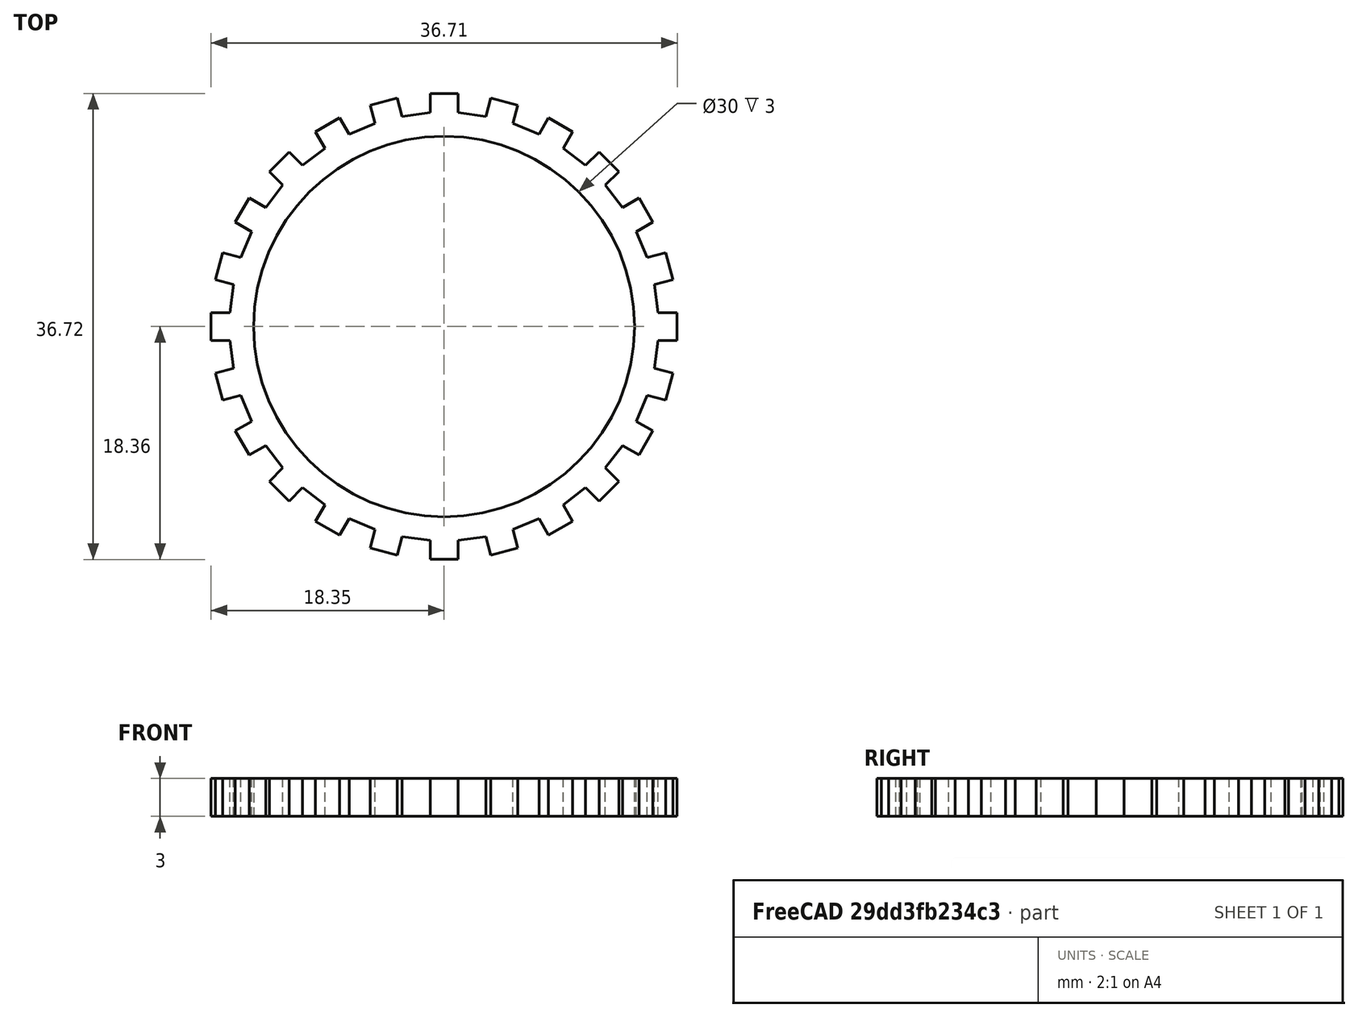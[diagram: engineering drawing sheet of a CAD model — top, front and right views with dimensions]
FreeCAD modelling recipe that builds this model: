
FCSTD DOCUMENT  (FreeCAD 0.19R24276 (Git))
Label: test_gear_1_1
License: All rights reserved
LicenseURL: http://en.wikipedia.org/wiki/All_rights_reserved
objects: Sketcher::SketchObject×1, PartDesign::Pad×1, PartDesign::Body×1
note: 4 computed .brp shape members not serialized (recipe doc carries the construction recipe); baked Part::Feature solids carry a one-line shape summary decoded from their .brp

FEATURE [Sketcher::SketchObject] Sketch
  FullyConstrained = false
  MapMode = 5
  Support = -> [XY_Plane]
  sketch-geometry (310):
    g0: Circle CenterX=0 CenterY=0 CenterZ=0 NormalX=0 NormalY=0 NormalZ=1 AngleXU=0 Radius=16.855
    g1: LineSegment StartX=0 StartY=16.855 StartZ=0 EndX=0 EndY=0 EndZ=0
    g2: LineSegment StartX=-4.3624 StartY=16.2807 StartZ=0 EndX=0 EndY=0 EndZ=0
    g3: LineSegment StartX=0 StartY=0 StartZ=0 EndX=4.3624 EndY=16.2807 EndZ=0
    g4: LineSegment StartX=0 StartY=0 StartZ=0 EndX=8.4275 EndY=14.5969 EndZ=0
    g5: LineSegment StartX=0 StartY=0 StartZ=0 EndX=11.9183 EndY=11.9183 EndZ=0
    g6: LineSegment StartX=0 StartY=0 StartZ=0 EndX=14.5969 EndY=8.4275 EndZ=0
    g7: LineSegment StartX=0 StartY=0 StartZ=0 EndX=16.2807 EndY=4.3624 EndZ=0
    g8: LineSegment StartX=0 StartY=0 StartZ=0 EndX=16.855 EndY=2.6e-15 EndZ=0
    g9: LineSegment StartX=-1.1 StartY=18.355 StartZ=0 EndX=-1.1 EndY=16.855 EndZ=0
    g10: LineSegment StartX=-1.1 StartY=16.855 StartZ=0 EndX=1.1 EndY=16.855 EndZ=0
    g11: LineSegment StartX=-1.1 StartY=18.355 StartZ=0 EndX=1.1 EndY=18.355 EndZ=0
    g12: GeomPoint X=0 Y=16.855 Z=0
    g13: LineSegment StartX=3.68811 StartY=18.0143 StartZ=0 EndX=3.29988 EndY=16.5654 EndZ=0
    g14: LineSegment StartX=3.29988 StartY=16.5654 StartZ=0 EndX=5.42491 EndY=15.996 EndZ=0
    g15: LineSegment StartX=3.68811 StartY=18.0143 StartZ=0 EndX=5.81314 EndY=17.4449 EndZ=0
    g16: LineSegment StartX=5.81314 StartY=17.4449 StartZ=0 EndX=5.42491 EndY=15.996 EndZ=0
    g17: GeomPoint X=4.3624 Y=16.2807 Z=0
    g18: LineSegment StartX=-10.1301 StartY=15.3459 StartZ=0 EndX=-9.38013 EndY=14.0469 EndZ=0
    g19: LineSegment StartX=-9.38013 StartY=14.0469 StartZ=0 EndX=-7.47487 EndY=15.1469 EndZ=0
    g20: LineSegment StartX=-10.1301 StartY=15.3459 StartZ=0 EndX=-8.22487 EndY=16.4459 EndZ=0
    g21: LineSegment StartX=-8.22487 StartY=16.4459 StartZ=0 EndX=-7.47487 EndY=15.1469 EndZ=0
    g22: GeomPoint X=-8.4275 Y=14.5969 Z=0
    g23: LineSegment StartX=0 StartY=0 StartZ=0 EndX=-8.4275 EndY=14.5969 EndZ=0
    g24: LineSegment StartX=-13.7568 StartY=12.2011 StartZ=0 EndX=-12.6961 EndY=11.1405 EndZ=0
    g25: LineSegment StartX=-12.6961 StartY=11.1405 StartZ=0 EndX=-11.1405 EndY=12.6961 EndZ=0
    g26: LineSegment StartX=-13.7568 StartY=12.2011 StartZ=0 EndX=-12.2011 EndY=13.7568 EndZ=0
    g27: LineSegment StartX=-12.2011 StartY=13.7568 StartZ=0 EndX=-11.1405 EndY=12.6961 EndZ=0
    g28: GeomPoint X=-11.9183 Y=11.9183 Z=0
    g29: LineSegment StartX=0 StartY=0 StartZ=0 EndX=-11.9183 EndY=11.9183 EndZ=0
    g30: LineSegment StartX=-5.81314 StartY=17.4449 StartZ=0 EndX=-5.42491 EndY=15.996 EndZ=0
    g31: LineSegment StartX=-5.42491 StartY=15.996 StartZ=0 EndX=-3.29988 EndY=16.5654 EndZ=0
    g32: LineSegment StartX=-5.81314 StartY=17.4449 StartZ=0 EndX=-3.68811 EndY=18.0143 EndZ=0
    g33: LineSegment StartX=-3.68811 StartY=18.0143 StartZ=0 EndX=-3.29988 EndY=16.5654 EndZ=0
    g34: GeomPoint X=-4.3624 Y=16.2807 Z=0
    g35: LineSegment StartX=8.22487 StartY=16.4459 StartZ=0 EndX=7.47487 EndY=15.1469 EndZ=0
    g36: LineSegment StartX=7.47487 StartY=15.1469 StartZ=0 EndX=9.38013 EndY=14.0469 EndZ=0
    g37: LineSegment StartX=8.22487 StartY=16.4459 StartZ=0 EndX=10.1301 EndY=15.3459 EndZ=0
    g38: LineSegment StartX=10.1301 StartY=15.3459 StartZ=0 EndX=9.38013 EndY=14.0469 EndZ=0
    g39: GeomPoint X=8.4275 Y=14.5969 Z=0
    g40: LineSegment StartX=12.2011 StartY=13.7568 StartZ=0 EndX=11.1405 EndY=12.6961 EndZ=0
    g41: LineSegment StartX=11.1405 StartY=12.6961 StartZ=0 EndX=12.6961 EndY=11.1405 EndZ=0
    g42: LineSegment StartX=12.2011 StartY=13.7568 StartZ=0 EndX=13.7568 EndY=12.2011 EndZ=0
    g43: LineSegment StartX=13.7568 StartY=12.2011 StartZ=0 EndX=12.6961 EndY=11.1405 EndZ=0
    g44: GeomPoint X=11.9183 Y=11.9183 Z=0
    g45: LineSegment StartX=15.3459 StartY=10.1301 StartZ=0 EndX=14.0469 EndY=9.38013 EndZ=0
    g46: LineSegment StartX=14.0469 StartY=9.38013 StartZ=0 EndX=15.1469 EndY=7.47487 EndZ=0
    g47: LineSegment StartX=15.3459 StartY=10.1301 StartZ=0 EndX=16.4459 EndY=8.22487 EndZ=0
    g48: LineSegment StartX=16.4459 StartY=8.22487 StartZ=0 EndX=15.1469 EndY=7.47487 EndZ=0
    g49: GeomPoint X=14.5969 Y=8.4275 Z=0
    g50: LineSegment StartX=17.4449 StartY=5.81314 StartZ=0 EndX=15.996 EndY=5.42491 EndZ=0
    g51: LineSegment StartX=15.996 StartY=5.42491 StartZ=0 EndX=16.5654 EndY=3.29988 EndZ=0
    g52: LineSegment StartX=17.4449 StartY=5.81314 StartZ=0 EndX=18.0143 EndY=3.68811 EndZ=0
    g53: LineSegment StartX=18.0143 StartY=3.68811 StartZ=0 EndX=16.5654 EndY=3.29988 EndZ=0
    g54: GeomPoint X=16.2807 Y=4.3624 Z=0
    g55: LineSegment StartX=0 StartY=0 StartZ=0 EndX=16.855 EndY=3.2e-15 EndZ=0
    g56: LineSegment StartX=18.355 StartY=1.1 StartZ=0 EndX=16.855 EndY=1.1 EndZ=0
    g57: LineSegment StartX=16.855 StartY=1.1 StartZ=0 EndX=16.855 EndY=-1.1 EndZ=0
    g58: LineSegment StartX=18.355 StartY=1.1 StartZ=0 EndX=18.355 EndY=-1.1 EndZ=0
    g59: LineSegment StartX=18.355 StartY=-1.1 StartZ=0 EndX=16.855 EndY=-1.1 EndZ=0
    g60: GeomPoint X=16.855 Y=3.2e-15 Z=0
    g61: LineSegment StartX=18.0143 StartY=-3.68811 StartZ=0 EndX=16.5654 EndY=-3.29988 EndZ=0
    g62: LineSegment StartX=16.5654 StartY=-3.29988 StartZ=0 EndX=15.996 EndY=-5.42491 EndZ=0
    g63: LineSegment StartX=18.0143 StartY=-3.68811 StartZ=0 EndX=17.4449 EndY=-5.81314 EndZ=0
    g64: LineSegment StartX=17.4449 StartY=-5.81314 StartZ=0 EndX=15.996 EndY=-5.42491 EndZ=0
    g65: GeomPoint X=16.2807 Y=-4.3624 Z=0
    g66: LineSegment StartX=0 StartY=0 StartZ=0 EndX=16.2807 EndY=-4.3624 EndZ=0
    g67: LineSegment StartX=16.4459 StartY=-8.22487 StartZ=0 EndX=15.1469 EndY=-7.47487 EndZ=0
    g68: LineSegment StartX=15.1469 StartY=-7.47487 StartZ=0 EndX=14.0469 EndY=-9.38013 EndZ=0
    g69: LineSegment StartX=16.4459 StartY=-8.22487 StartZ=0 EndX=15.3459 EndY=-10.1301 EndZ=0
    g70: LineSegment StartX=15.3459 StartY=-10.1301 StartZ=0 EndX=14.0469 EndY=-9.38013 EndZ=0
    g71: GeomPoint X=14.5969 Y=-8.4275 Z=0
    g72: LineSegment StartX=0 StartY=0 StartZ=0 EndX=14.5969 EndY=-8.4275 EndZ=0
    g73: LineSegment StartX=-16.4459 StartY=8.22487 StartZ=0 EndX=-15.1469 EndY=7.47487 EndZ=0
    g74: LineSegment StartX=-15.1469 StartY=7.47487 StartZ=0 EndX=-14.0469 EndY=9.38013 EndZ=0
    g75: LineSegment StartX=-16.4459 StartY=8.22487 StartZ=0 EndX=-15.3459 EndY=10.1301 EndZ=0
    g76: LineSegment StartX=-15.3459 StartY=10.1301 StartZ=0 EndX=-14.0469 EndY=9.38013 EndZ=0
    g77: GeomPoint X=-14.5969 Y=8.4275 Z=0
    g78: LineSegment StartX=0 StartY=0 StartZ=0 EndX=-14.5969 EndY=8.4275 EndZ=0
    g79: LineSegment StartX=-15.1469 StartY=7.47487 StartZ=0 EndX=-16.4459 EndY=8.22487 EndZ=0
    g80: LineSegment StartX=-16.4459 StartY=8.22487 StartZ=0 EndX=-15.3459 EndY=10.1301 EndZ=0
    g81: LineSegment StartX=-15.3459 StartY=10.1301 StartZ=0 EndX=-14.0469 EndY=9.38013 EndZ=0
    g82: LineSegment StartX=-12.6961 StartY=11.1405 StartZ=0 EndX=-14.0469 EndY=9.38013 EndZ=0
    g83: LineSegment StartX=-12.6961 StartY=11.1405 StartZ=0 EndX=-13.7568 EndY=12.2011 EndZ=0
    g84: LineSegment StartX=-13.7568 StartY=12.2011 StartZ=0 EndX=-12.2011 EndY=13.7568 EndZ=0
    g85: LineSegment StartX=-12.2011 StartY=13.7568 StartZ=0 EndX=-11.1405 EndY=12.6961 EndZ=0
    g86: LineSegment StartX=-11.1405 StartY=12.6961 StartZ=0 EndX=-9.38013 EndY=14.0469 EndZ=0
    g87: LineSegment StartX=-9.38013 StartY=14.0469 StartZ=0 EndX=-10.1301 EndY=15.3459 EndZ=0
    g88: LineSegment StartX=-10.1301 StartY=15.3459 StartZ=0 EndX=-8.22487 EndY=16.4459 EndZ=0
    g89: LineSegment StartX=-8.22487 StartY=16.4459 StartZ=0 EndX=-7.47487 EndY=15.1469 EndZ=0
    g90: LineSegment StartX=-7.47487 StartY=15.1469 StartZ=0 EndX=-5.42491 EndY=15.996 EndZ=0
    g91: LineSegment StartX=-5.42491 StartY=15.996 StartZ=0 EndX=-5.81314 EndY=17.4449 EndZ=0
    g92: LineSegment StartX=-5.81314 StartY=17.4449 StartZ=0 EndX=-3.68811 EndY=18.0143 EndZ=0
    g93: LineSegment StartX=-3.68811 StartY=18.0143 StartZ=0 EndX=-3.29988 EndY=16.5654 EndZ=0
    g94: LineSegment StartX=-3.29988 StartY=16.5654 StartZ=0 EndX=-1.1 EndY=16.855 EndZ=0
    g95: LineSegment StartX=-1.1 StartY=16.855 StartZ=0 EndX=-1.1 EndY=18.355 EndZ=0
    g96: LineSegment StartX=-1.1 StartY=18.355 StartZ=0 EndX=1.1 EndY=18.355 EndZ=0
    g97: LineSegment StartX=-18.0156 StartY=3.68811 StartZ=0 EndX=-16.5667 EndY=3.29988 EndZ=0
    g98: LineSegment StartX=-16.5667 StartY=3.29988 StartZ=0 EndX=-15.9973 EndY=5.42491 EndZ=0
    g99: LineSegment StartX=-18.0156 StartY=3.68811 StartZ=0 EndX=-17.4462 EndY=5.81314 EndZ=0
    g100: LineSegment StartX=-17.4462 StartY=5.81314 StartZ=0 EndX=-15.9973 EndY=5.42491 EndZ=0
    g101: GeomPoint X=-16.282 Y=4.3624 Z=0
    g102: LineSegment StartX=-0.00134425 StartY=1.8e-15 StartZ=0 EndX=-16.282 EndY=4.3624 EndZ=0
    g103: LineSegment StartX=-16.5667 StartY=3.29988 StartZ=0 EndX=-18.0156 EndY=3.68811 EndZ=0
    g104: LineSegment StartX=-18.0156 StartY=3.68811 StartZ=0 EndX=-17.4462 EndY=5.81314 EndZ=0
    g105: LineSegment StartX=-17.4462 StartY=5.81314 StartZ=0 EndX=-15.9973 EndY=5.42491 EndZ=0
    g106: LineSegment StartX=-18.3549 StartY=-1.1 StartZ=0 EndX=-16.8549 EndY=-1.1 EndZ=0
    g107: LineSegment StartX=-16.8549 StartY=-1.1 StartZ=0 EndX=-16.8549 EndY=1.1 EndZ=0
    g108: LineSegment StartX=-18.3549 StartY=-1.1 StartZ=0 EndX=-18.3549 EndY=1.1 EndZ=0
    g109: LineSegment StartX=-18.3549 StartY=1.1 StartZ=0 EndX=-16.8549 EndY=1.1 EndZ=0
    g110: GeomPoint X=-16.8549 Y=-6.7e-15 Z=0
    g111: LineSegment StartX=9.05985e-05 StartY=2.3e-15 StartZ=0 EndX=-16.8549 EndY=-6.7e-15 EndZ=0
    g112: LineSegment StartX=-18.3549 StartY=-1.1 StartZ=0 EndX=-18.3549 EndY=1.1 EndZ=0
    g113: LineSegment StartX=-18.3549 StartY=1.1 StartZ=0 EndX=-16.8549 EndY=1.1 EndZ=0
    g114: LineSegment StartX=-15.1469 StartY=7.47487 StartZ=0 EndX=-15.9973 EndY=5.42491 EndZ=0
    g115: LineSegment StartX=-16.5667 StartY=3.29988 StartZ=0 EndX=-16.8549 EndY=1.1 EndZ=0
    g116: LineSegment StartX=4.3624 StartY=16.2807 StartZ=0 EndX=0 EndY=0 EndZ=0
    g117: LineSegment StartX=1.1 StartY=18.355 StartZ=0 EndX=1.1 EndY=16.855 EndZ=0
    g118: GeomPoint X=0 Y=16.855 Z=0
    g119: LineSegment StartX=10.1301 StartY=15.3459 StartZ=0 EndX=9.38013 EndY=14.0469 EndZ=0
    g120: LineSegment StartX=9.38013 StartY=14.0469 StartZ=0 EndX=7.47487 EndY=15.1469 EndZ=0
    g121: LineSegment StartX=10.1301 StartY=15.3459 StartZ=0 EndX=8.22487 EndY=16.4459 EndZ=0
    g122: LineSegment StartX=8.22487 StartY=16.4459 StartZ=0 EndX=7.47487 EndY=15.1469 EndZ=0
    g123: GeomPoint X=8.4275 Y=14.5969 Z=0
    g124: LineSegment StartX=0 StartY=0 StartZ=0 EndX=8.4275 EndY=14.5969 EndZ=0
    g125: LineSegment StartX=13.7568 StartY=12.2011 StartZ=0 EndX=12.6961 EndY=11.1405 EndZ=0
    g126: LineSegment StartX=12.6961 StartY=11.1405 StartZ=0 EndX=11.1405 EndY=12.6961 EndZ=0
    g127: LineSegment StartX=13.7568 StartY=12.2011 StartZ=0 EndX=12.2011 EndY=13.7568 EndZ=0
    g128: LineSegment StartX=12.2011 StartY=13.7568 StartZ=0 EndX=11.1405 EndY=12.6961 EndZ=0
    g129: GeomPoint X=11.9183 Y=11.9183 Z=0
    g130: LineSegment StartX=0 StartY=0 StartZ=0 EndX=11.9183 EndY=11.9183 EndZ=0
    g131: LineSegment StartX=5.81314 StartY=17.4449 StartZ=0 EndX=5.42491 EndY=15.996 EndZ=0
    g132: LineSegment StartX=5.42491 StartY=15.996 StartZ=0 EndX=3.29988 EndY=16.5654 EndZ=0
    g133: LineSegment StartX=5.81314 StartY=17.4449 StartZ=0 EndX=3.68811 EndY=18.0143 EndZ=0
    g134: LineSegment StartX=3.68811 StartY=18.0143 StartZ=0 EndX=3.29988 EndY=16.5654 EndZ=0
    g135: GeomPoint X=4.3624 Y=16.2807 Z=0
    g136: LineSegment StartX=16.4459 StartY=8.22487 StartZ=0 EndX=15.1469 EndY=7.47487 EndZ=0
    g137: LineSegment StartX=15.1469 StartY=7.47487 StartZ=0 EndX=14.0469 EndY=9.38013 EndZ=0
    g138: LineSegment StartX=16.4459 StartY=8.22487 StartZ=0 EndX=15.3459 EndY=10.1301 EndZ=0
    g139: LineSegment StartX=15.3459 StartY=10.1301 StartZ=0 EndX=14.0469 EndY=9.38013 EndZ=0
    g140: GeomPoint X=14.5969 Y=8.4275 Z=0
    g141: LineSegment StartX=0 StartY=0 StartZ=0 EndX=14.5969 EndY=8.4275 EndZ=0
    g142: LineSegment StartX=15.1469 StartY=7.47487 StartZ=0 EndX=16.4459 EndY=8.22487 EndZ=0
    g143: LineSegment StartX=16.4459 StartY=8.22487 StartZ=0 EndX=15.3459 EndY=10.1301 EndZ=0
    g144: LineSegment StartX=15.3459 StartY=10.1301 StartZ=0 EndX=14.0469 EndY=9.38013 EndZ=0
    g145: LineSegment StartX=12.6961 StartY=11.1405 StartZ=0 EndX=14.0469 EndY=9.38013 EndZ=0
    g146: LineSegment StartX=12.6961 StartY=11.1405 StartZ=0 EndX=13.7568 EndY=12.2011 EndZ=0
    g147: LineSegment StartX=13.7568 StartY=12.2011 StartZ=0 EndX=12.2011 EndY=13.7568 EndZ=0
    g148: LineSegment StartX=12.2011 StartY=13.7568 StartZ=0 EndX=11.1405 EndY=12.6961 EndZ=0
    g149: LineSegment StartX=11.1405 StartY=12.6961 StartZ=0 EndX=9.38013 EndY=14.0469 EndZ=0
    g150: LineSegment StartX=9.38013 StartY=14.0469 StartZ=0 EndX=10.1301 EndY=15.3459 EndZ=0
    g151: LineSegment StartX=10.1301 StartY=15.3459 StartZ=0 EndX=8.22487 EndY=16.4459 EndZ=0
    g152: LineSegment StartX=8.22487 StartY=16.4459 StartZ=0 EndX=7.47487 EndY=15.1469 EndZ=0
    g153: LineSegment StartX=7.47487 StartY=15.1469 StartZ=0 EndX=5.42491 EndY=15.996 EndZ=0
    g154: LineSegment StartX=5.42491 StartY=15.996 StartZ=0 EndX=5.81314 EndY=17.4449 EndZ=0
    g155: LineSegment StartX=5.81314 StartY=17.4449 StartZ=0 EndX=3.68811 EndY=18.0143 EndZ=0
    g156: LineSegment StartX=3.68811 StartY=18.0143 StartZ=0 EndX=3.29988 EndY=16.5654 EndZ=0
    g157: LineSegment StartX=3.29988 StartY=16.5654 StartZ=0 EndX=1.1 EndY=16.855 EndZ=0
    g158: LineSegment StartX=18.0156 StartY=3.68811 StartZ=0 EndX=16.5667 EndY=3.29988 EndZ=0
    g159: LineSegment StartX=16.5667 StartY=3.29988 StartZ=0 EndX=15.9973 EndY=5.42491 EndZ=0
    g160: LineSegment StartX=18.0156 StartY=3.68811 StartZ=0 EndX=17.4462 EndY=5.81314 EndZ=0
    g161: LineSegment StartX=17.4462 StartY=5.81314 StartZ=0 EndX=15.9973 EndY=5.42491 EndZ=0
    g162: GeomPoint X=16.282 Y=4.3624 Z=0
    g163: LineSegment StartX=0.00134425 StartY=-1.2e-15 StartZ=0 EndX=16.282 EndY=4.3624 EndZ=0
    g164: LineSegment StartX=17.4462 StartY=5.81314 StartZ=0 EndX=15.9973 EndY=5.42491 EndZ=0
    g165: LineSegment StartX=18.3549 StartY=-1.1 StartZ=0 EndX=16.8549 EndY=-1.1 EndZ=0
    g166: LineSegment StartX=16.8549 StartY=-1.1 StartZ=0 EndX=16.8549 EndY=1.1 EndZ=0
    g167: LineSegment StartX=18.3549 StartY=-1.1 StartZ=0 EndX=18.3549 EndY=1.1 EndZ=0
    g168: LineSegment StartX=18.3549 StartY=1.1 StartZ=0 EndX=16.8549 EndY=1.1 EndZ=0
    g169: GeomPoint X=16.8549 Y=-7.1e-15 Z=0
    g170: LineSegment StartX=-9.05985e-05 StartY=1.7e-15 StartZ=0 EndX=16.8549 EndY=-7.1e-15 EndZ=0
    g171: LineSegment StartX=18.3549 StartY=1.1 StartZ=0 EndX=16.8549 EndY=1.1 EndZ=0
    g172: LineSegment StartX=15.1469 StartY=7.47487 StartZ=0 EndX=15.9973 EndY=5.42491 EndZ=0
    g173: LineSegment StartX=16.5667 StartY=3.29988 StartZ=0 EndX=16.8549 EndY=1.1 EndZ=0
    g174: LineSegment StartX=1.1 StartY=16.855 StartZ=0 EndX=1.1 EndY=18.355 EndZ=0
    g175: LineSegment StartX=-1.1 StartY=-18.355 StartZ=0 EndX=-1.1 EndY=-16.855 EndZ=0
    g176: LineSegment StartX=-1.1 StartY=-16.855 StartZ=0 EndX=1.1 EndY=-16.855 EndZ=0
    g177: LineSegment StartX=-1.1 StartY=-18.355 StartZ=0 EndX=1.1 EndY=-18.355 EndZ=0
    g178: GeomPoint X=1.08e-14 Y=-16.855 Z=0
    g179: LineSegment StartX=3.68811 StartY=-18.0143 StartZ=0 EndX=3.29988 EndY=-16.5654 EndZ=0
    g180: LineSegment StartX=3.29988 StartY=-16.5654 StartZ=0 EndX=5.42491 EndY=-15.996 EndZ=0
    g181: LineSegment StartX=3.68811 StartY=-18.0143 StartZ=0 EndX=5.81314 EndY=-17.4449 EndZ=0
    g182: LineSegment StartX=5.81314 StartY=-17.4449 StartZ=0 EndX=5.42491 EndY=-15.996 EndZ=0
    g183: GeomPoint X=4.3624 Y=-16.2807 Z=0
    g184: LineSegment StartX=-10.1301 StartY=-15.3459 StartZ=0 EndX=-9.38013 EndY=-14.0469 EndZ=0
    g185: LineSegment StartX=-9.38013 StartY=-14.0469 StartZ=0 EndX=-7.47487 EndY=-15.1469 EndZ=0
    g186: LineSegment StartX=-10.1301 StartY=-15.3459 StartZ=0 EndX=-8.22487 EndY=-16.4459 EndZ=0
    g187: LineSegment StartX=-8.22487 StartY=-16.4459 StartZ=0 EndX=-7.47487 EndY=-15.1469 EndZ=0
    g188: GeomPoint X=-8.4275 Y=-14.5969 Z=0
    g189: LineSegment StartX=-13.7568 StartY=-12.2011 StartZ=0 EndX=-12.6961 EndY=-11.1405 EndZ=0
    g190: LineSegment StartX=-12.6961 StartY=-11.1405 StartZ=0 EndX=-11.1405 EndY=-12.6961 EndZ=0
    g191: LineSegment StartX=-13.7568 StartY=-12.2011 StartZ=0 EndX=-12.2011 EndY=-13.7568 EndZ=0
    g192: LineSegment StartX=-12.2011 StartY=-13.7568 StartZ=0 EndX=-11.1405 EndY=-12.6961 EndZ=0
    g193: GeomPoint X=-11.9183 Y=-11.9183 Z=0
    g194: LineSegment StartX=-5.81314 StartY=-17.4449 StartZ=0 EndX=-5.42491 EndY=-15.996 EndZ=0
    g195: LineSegment StartX=-5.42491 StartY=-15.996 StartZ=0 EndX=-3.29988 EndY=-16.5654 EndZ=0
    g196: LineSegment StartX=-5.81314 StartY=-17.4449 StartZ=0 EndX=-3.68811 EndY=-18.0143 EndZ=0
    g197: LineSegment StartX=-3.68811 StartY=-18.0143 StartZ=0 EndX=-3.29988 EndY=-16.5654 EndZ=0
    g198: GeomPoint X=-4.3624 Y=-16.2807 Z=0
    g199: LineSegment StartX=8.22487 StartY=-16.4459 StartZ=0 EndX=7.47487 EndY=-15.1469 EndZ=0
    g200: LineSegment StartX=7.47487 StartY=-15.1469 StartZ=0 EndX=9.38013 EndY=-14.0469 EndZ=0
    g201: LineSegment StartX=8.22487 StartY=-16.4459 StartZ=0 EndX=10.1301 EndY=-15.3459 EndZ=0
    g202: LineSegment StartX=10.1301 StartY=-15.3459 StartZ=0 EndX=9.38013 EndY=-14.0469 EndZ=0
    g203: GeomPoint X=8.4275 Y=-14.5969 Z=0
    g204: LineSegment StartX=12.2011 StartY=-13.7568 StartZ=0 EndX=11.1405 EndY=-12.6961 EndZ=0
    g205: LineSegment StartX=11.1405 StartY=-12.6961 StartZ=0 EndX=12.6961 EndY=-11.1405 EndZ=0
    g206: LineSegment StartX=12.2011 StartY=-13.7568 StartZ=0 EndX=13.7568 EndY=-12.2011 EndZ=0
    g207: LineSegment StartX=13.7568 StartY=-12.2011 StartZ=0 EndX=12.6961 EndY=-11.1405 EndZ=0
    g208: GeomPoint X=11.9183 Y=-11.9183 Z=0
    g209: LineSegment StartX=15.3459 StartY=-10.1301 StartZ=0 EndX=14.0469 EndY=-9.38013 EndZ=0
    g210: LineSegment StartX=14.0469 StartY=-9.38013 StartZ=0 EndX=15.1469 EndY=-7.47487 EndZ=0
    g211: LineSegment StartX=15.3459 StartY=-10.1301 StartZ=0 EndX=16.4459 EndY=-8.22487 EndZ=0
    g212: LineSegment StartX=16.4459 StartY=-8.22487 StartZ=0 EndX=15.1469 EndY=-7.47487 EndZ=0
    g213: GeomPoint X=14.5969 Y=-8.4275 Z=0
    g214: LineSegment StartX=17.4449 StartY=-5.81314 StartZ=0 EndX=15.996 EndY=-5.42491 EndZ=0
    g215: LineSegment StartX=15.996 StartY=-5.42491 StartZ=0 EndX=16.5654 EndY=-3.29988 EndZ=0
    g216: LineSegment StartX=17.4449 StartY=-5.81314 StartZ=0 EndX=18.0143 EndY=-3.68811 EndZ=0
    g217: LineSegment StartX=18.0143 StartY=-3.68811 StartZ=0 EndX=16.5654 EndY=-3.29988 EndZ=0
    g218: GeomPoint X=16.2807 Y=-4.3624 Z=0
    g219: LineSegment StartX=18.355 StartY=-1.1 StartZ=0 EndX=16.855 EndY=-1.1 EndZ=0
    g220: LineSegment StartX=-16.4459 StartY=-8.22487 StartZ=0 EndX=-15.1469 EndY=-7.47487 EndZ=0
    g221: LineSegment StartX=-15.1469 StartY=-7.47487 StartZ=0 EndX=-14.0469 EndY=-9.38013 EndZ=0
    g222: LineSegment StartX=-16.4459 StartY=-8.22487 StartZ=0 EndX=-15.3459 EndY=-10.1301 EndZ=0
    g223: LineSegment StartX=-15.3459 StartY=-10.1301 StartZ=0 EndX=-14.0469 EndY=-9.38013 EndZ=0
    g224: GeomPoint X=-14.5969 Y=-8.4275 Z=0
    g225: LineSegment StartX=-15.1469 StartY=-7.47487 StartZ=0 EndX=-16.4459 EndY=-8.22487 EndZ=0
    g226: LineSegment StartX=-16.4459 StartY=-8.22487 StartZ=0 EndX=-15.3459 EndY=-10.1301 EndZ=0
    g227: LineSegment StartX=-15.3459 StartY=-10.1301 StartZ=0 EndX=-14.0469 EndY=-9.38013 EndZ=0
    g228: LineSegment StartX=-12.6961 StartY=-11.1405 StartZ=0 EndX=-14.0469 EndY=-9.38013 EndZ=0
    g229: LineSegment StartX=-12.6961 StartY=-11.1405 StartZ=0 EndX=-13.7568 EndY=-12.2011 EndZ=0
    g230: LineSegment StartX=-13.7568 StartY=-12.2011 StartZ=0 EndX=-12.2011 EndY=-13.7568 EndZ=0
    g231: LineSegment StartX=-12.2011 StartY=-13.7568 StartZ=0 EndX=-11.1405 EndY=-12.6961 EndZ=0
    g232: LineSegment StartX=-11.1405 StartY=-12.6961 StartZ=0 EndX=-9.38013 EndY=-14.0469 EndZ=0
    g233: LineSegment StartX=-9.38013 StartY=-14.0469 StartZ=0 EndX=-10.1301 EndY=-15.3459 EndZ=0
    g234: LineSegment StartX=-10.1301 StartY=-15.3459 StartZ=0 EndX=-8.22487 EndY=-16.4459 EndZ=0
    g235: LineSegment StartX=-8.22487 StartY=-16.4459 StartZ=0 EndX=-7.47487 EndY=-15.1469 EndZ=0
    g236: LineSegment StartX=-7.47487 StartY=-15.1469 StartZ=0 EndX=-5.42491 EndY=-15.996 EndZ=0
    g237: LineSegment StartX=-5.42491 StartY=-15.996 StartZ=0 EndX=-5.81314 EndY=-17.4449 EndZ=0
    g238: LineSegment StartX=-5.81314 StartY=-17.4449 StartZ=0 EndX=-3.68811 EndY=-18.0143 EndZ=0
    g239: LineSegment StartX=-3.68811 StartY=-18.0143 StartZ=0 EndX=-3.29988 EndY=-16.5654 EndZ=0
    g240: LineSegment StartX=-3.29988 StartY=-16.5654 StartZ=0 EndX=-1.1 EndY=-16.855 EndZ=0
    g241: LineSegment StartX=-1.1 StartY=-16.855 StartZ=0 EndX=-1.1 EndY=-18.355 EndZ=0
    g242: LineSegment StartX=-1.1 StartY=-18.355 StartZ=0 EndX=1.1 EndY=-18.355 EndZ=0
    g243: LineSegment StartX=-18.0156 StartY=-3.68811 StartZ=0 EndX=-16.5667 EndY=-3.29988 EndZ=0
    g244: LineSegment StartX=-16.5667 StartY=-3.29988 StartZ=0 EndX=-15.9973 EndY=-5.42491 EndZ=0
    g245: LineSegment StartX=-18.0156 StartY=-3.68811 StartZ=0 EndX=-17.4462 EndY=-5.81314 EndZ=0
    g246: LineSegment StartX=-17.4462 StartY=-5.81314 StartZ=0 EndX=-15.9973 EndY=-5.42491 EndZ=0
    g247: GeomPoint X=-16.282 Y=-4.3624 Z=0
    g248: LineSegment StartX=-16.5667 StartY=-3.29988 StartZ=0 EndX=-18.0156 EndY=-3.68811 EndZ=0
    g249: LineSegment StartX=-18.0156 StartY=-3.68811 StartZ=0 EndX=-17.4462 EndY=-5.81314 EndZ=0
    g250: LineSegment StartX=-17.4462 StartY=-5.81314 StartZ=0 EndX=-15.9973 EndY=-5.42491 EndZ=0
    g251: LineSegment StartX=-18.3549 StartY=-1.1 StartZ=0 EndX=-16.8549 EndY=-1.1 EndZ=0
    g252: LineSegment StartX=-18.3549 StartY=-1.1 StartZ=0 EndX=-16.8549 EndY=-1.1 EndZ=0
    g253: LineSegment StartX=-15.1469 StartY=-7.47487 StartZ=0 EndX=-15.9973 EndY=-5.42491 EndZ=0
    g254: LineSegment StartX=-16.5667 StartY=-3.29988 StartZ=0 EndX=-16.8549 EndY=-1.1 EndZ=0
    g255: LineSegment StartX=1.1 StartY=-18.355 StartZ=0 EndX=1.1 EndY=-16.855 EndZ=0
    g256: GeomPoint X=1.08e-14 Y=-16.855 Z=0
    g257: LineSegment StartX=10.1301 StartY=-15.3459 StartZ=0 EndX=9.38013 EndY=-14.0469 EndZ=0
    g258: LineSegment StartX=9.38013 StartY=-14.0469 StartZ=0 EndX=7.47487 EndY=-15.1469 EndZ=0
    g259: LineSegment StartX=10.1301 StartY=-15.3459 StartZ=0 EndX=8.22487 EndY=-16.4459 EndZ=0
    g260: LineSegment StartX=8.22487 StartY=-16.4459 StartZ=0 EndX=7.47487 EndY=-15.1469 EndZ=0
    g261: GeomPoint X=8.4275 Y=-14.5969 Z=0
    g262: LineSegment StartX=13.7568 StartY=-12.2011 StartZ=0 EndX=12.6961 EndY=-11.1405 EndZ=0
    g263: LineSegment StartX=12.6961 StartY=-11.1405 StartZ=0 EndX=11.1405 EndY=-12.6961 EndZ=0
    g264: LineSegment StartX=13.7568 StartY=-12.2011 StartZ=0 EndX=12.2011 EndY=-13.7568 EndZ=0
    g265: LineSegment StartX=12.2011 StartY=-13.7568 StartZ=0 EndX=11.1405 EndY=-12.6961 EndZ=0
    g266: GeomPoint X=11.9183 Y=-11.9183 Z=0
    g267: LineSegment StartX=5.81314 StartY=-17.4449 StartZ=0 EndX=5.42491 EndY=-15.996 EndZ=0
    g268: LineSegment StartX=5.42491 StartY=-15.996 StartZ=0 EndX=3.29988 EndY=-16.5654 EndZ=0
    g269: LineSegment StartX=5.81314 StartY=-17.4449 StartZ=0 EndX=3.68811 EndY=-18.0143 EndZ=0
    g270: LineSegment StartX=3.68811 StartY=-18.0143 StartZ=0 EndX=3.29988 EndY=-16.5654 EndZ=0
    g271: GeomPoint X=4.3624 Y=-16.2807 Z=0
    g272: LineSegment StartX=16.4459 StartY=-8.22487 StartZ=0 EndX=15.1469 EndY=-7.47487 EndZ=0
    g273: LineSegment StartX=15.1469 StartY=-7.47487 StartZ=0 EndX=14.0469 EndY=-9.38013 EndZ=0
    g274: LineSegment StartX=16.4459 StartY=-8.22487 StartZ=0 EndX=15.3459 EndY=-10.1301 EndZ=0
    g275: LineSegment StartX=15.3459 StartY=-10.1301 StartZ=0 EndX=14.0469 EndY=-9.38013 EndZ=0
    g276: GeomPoint X=14.5969 Y=-8.4275 Z=0
    g277: LineSegment StartX=15.1469 StartY=-7.47487 StartZ=0 EndX=16.4459 EndY=-8.22487 EndZ=0
    g278: LineSegment StartX=16.4459 StartY=-8.22487 StartZ=0 EndX=15.3459 EndY=-10.1301 EndZ=0
    g279: LineSegment StartX=15.3459 StartY=-10.1301 StartZ=0 EndX=14.0469 EndY=-9.38013 EndZ=0
    g280: LineSegment StartX=12.6961 StartY=-11.1405 StartZ=0 EndX=14.0469 EndY=-9.38013 EndZ=0
    g281: LineSegment StartX=12.6961 StartY=-11.1405 StartZ=0 EndX=13.7568 EndY=-12.2011 EndZ=0
    g282: LineSegment StartX=13.7568 StartY=-12.2011 StartZ=0 EndX=12.2011 EndY=-13.7568 EndZ=0
    g283: LineSegment StartX=12.2011 StartY=-13.7568 StartZ=0 EndX=11.1405 EndY=-12.6961 EndZ=0
    g284: LineSegment StartX=11.1405 StartY=-12.6961 StartZ=0 EndX=9.38013 EndY=-14.0469 EndZ=0
    g285: LineSegment StartX=9.38013 StartY=-14.0469 StartZ=0 EndX=10.1301 EndY=-15.3459 EndZ=0
    g286: LineSegment StartX=10.1301 StartY=-15.3459 StartZ=0 EndX=8.22487 EndY=-16.4459 EndZ=0
    g287: LineSegment StartX=8.22487 StartY=-16.4459 StartZ=0 EndX=7.47487 EndY=-15.1469 EndZ=0
    g288: LineSegment StartX=7.47487 StartY=-15.1469 StartZ=0 EndX=5.42491 EndY=-15.996 EndZ=0
    g289: LineSegment StartX=5.42491 StartY=-15.996 StartZ=0 EndX=5.81314 EndY=-17.4449 EndZ=0
    g290: LineSegment StartX=5.81314 StartY=-17.4449 StartZ=0 EndX=3.68811 EndY=-18.0143 EndZ=0
    g291: LineSegment StartX=3.68811 StartY=-18.0143 StartZ=0 EndX=3.29988 EndY=-16.5654 EndZ=0
    g292: LineSegment StartX=3.29988 StartY=-16.5654 StartZ=0 EndX=1.1 EndY=-16.855 EndZ=0
    g293: LineSegment StartX=18.0156 StartY=-3.68811 StartZ=0 EndX=16.5667 EndY=-3.29988 EndZ=0
    g294: LineSegment StartX=16.5667 StartY=-3.29988 StartZ=0 EndX=15.9973 EndY=-5.42491 EndZ=0
    g295: LineSegment StartX=18.0156 StartY=-3.68811 StartZ=0 EndX=17.4462 EndY=-5.81314 EndZ=0
    g296: LineSegment StartX=17.4462 StartY=-5.81314 StartZ=0 EndX=15.9973 EndY=-5.42491 EndZ=0
    g297: GeomPoint X=16.282 Y=-4.3624 Z=0
    g298: LineSegment StartX=16.5667 StartY=-3.29988 StartZ=0 EndX=18.0156 EndY=-3.68811 EndZ=0
    g299: LineSegment StartX=18.0156 StartY=-3.68811 StartZ=0 EndX=17.4462 EndY=-5.81314 EndZ=0
    g300: LineSegment StartX=17.4462 StartY=-5.81314 StartZ=0 EndX=15.9973 EndY=-5.42491 EndZ=0
    g301: LineSegment StartX=18.3549 StartY=-1.1 StartZ=0 EndX=16.8549 EndY=-1.1 EndZ=0
    g302: LineSegment StartX=15.1469 StartY=-7.47487 StartZ=0 EndX=15.9973 EndY=-5.42491 EndZ=0
    g303: LineSegment StartX=16.5667 StartY=-3.29988 StartZ=0 EndX=16.8549 EndY=-1.1 EndZ=0
    g304: LineSegment StartX=1.1 StartY=-16.855 StartZ=0 EndX=1.1 EndY=-18.355 EndZ=0
    g305: Circle CenterX=0 CenterY=0 CenterZ=0 NormalX=0 NormalY=0 NormalZ=1 AngleXU=0 Radius=15
    g306: LineSegment StartX=18.0156 StartY=3.68811 StartZ=0 EndX=16.5667 EndY=3.29988 EndZ=0
    g307: LineSegment StartX=17.4462 StartY=5.81314 StartZ=0 EndX=18.0156 EndY=3.68811 EndZ=0
    g308: LineSegment StartX=18.3549 StartY=1.1 StartZ=0 EndX=18.355 EndY=-1.1 EndZ=0
    g309: LineSegment StartX=18.355 StartY=-1.1 StartZ=0 EndX=16.8549 EndY=-1.1 EndZ=0
  constraints (689):
    c: Diameter(g0) = 33.71
    c: Vertical(g1)
    c: Coincident(g0,g-1)
    c: Coincident(g1,g0)
    c: Coincident(g2,g0)
    c: Angle(g1,g2) = 0.261799
    c: Coincident(g3,g0)
    c: Angle(g3,g1) = 0.261799
    c: PointOnObject(g3,g0)
    c: PointOnObject(g1,g0)
    c: PointOnObject(g2,g0)
    c: Coincident(g4,g0)
    c: Angle(g4,g3) = 0.261799
    c: PointOnObject(g4,g0)
    c: Coincident(g5,g0)
    c: Angle(g5,g4) = 0.261799
    c: Coincident(g6,g0)
    c: Angle(g6,g5) = 0.261799
    c: Coincident(g7,g0)
    c: Angle(g7,g6) = 0.261799
    c: Coincident(g8,g0)
    c: Angle(g8,g7) = 0.261799
    c: PointOnObject(g5,g0)
    c: PointOnObject(g7,g0)
    c: PointOnObject(g6,g0)
    c: PointOnObject(g8,g0)
    c: Coincident(g10,g9)
    c: Coincident(g11,g9)
    c: Parallel(g10,g11)
    c: Perpendicular(g10,g9)
    c: Distance(g9,g11) = 2.2
    c: Distance(g11,g10) = 1.5
    c: PointOnObject(g12,g10)
    c: Distance(g9,g12) = 1.1
    c: Coincident(g12,g1)
    c: Perpendicular(g1,g10)
    c: Coincident(g14,g13)
    c: Coincident(g15,g13)
    c: Coincident(g16,g15)
    c: Coincident(g16,g14)
    c: Parallel(g14,g15)
    c: Parallel(g13,g16)
    c: Perpendicular(g14,g13)
    c: Distance(g13,g15) = 2.2
    c: Distance(g15,g14) = 1.5
    c: PointOnObject(g17,g14)
    c: Distance(g13,g17) = 1.1
    c: Coincident(g17,g3)
    c: Perpendicular(g3,g14)
    c: Coincident(g19,g18)
    c: Coincident(g20,g18)
    c: Coincident(g21,g20)
    c: Coincident(g21,g19)
    c: Parallel(g19,g20)
    c: Parallel(g18,g21)
    c: Perpendicular(g19,g18)
    c: Distance(g18,g20) = 2.2
    c: Distance(g20,g19) = 1.5
    c: PointOnObject(g22,g19)
    c: Distance(g18,g22) = 1.1
    c: Perpendicular(g23,g19)
    c: Coincident(g23,g0)
    c: Angle(g23,g2) = -0.261799
    c: PointOnObject(g23,g0)
    c: Coincident(g22,g23)
    c: Coincident(g25,g24)
    c: Coincident(g26,g24)
    c: Coincident(g27,g26)
    c: Coincident(g27,g25)
    c: Parallel(g25,g26)
    c: Parallel(g24,g27)
    c: Perpendicular(g25,g24)
    c: Distance(g24,g26) = 2.2
    c: Distance(g26,g25) = 1.5
    c: PointOnObject(g28,g25)
    c: Distance(g24,g28) = 1.1
    c: Perpendicular(g29,g25)
    c: Coincident(g28,g29)
    c: Equal(g29,g23)
    c: Coincident(g29,g0)
    c: Angle(g23,g29) = 0.261799
    c: Coincident(g31,g30)
    c: Coincident(g32,g30)
    c: Coincident(g33,g32)
    c: Coincident(g33,g31)
    c: Parallel(g31,g32)
    c: Parallel(g30,g33)
    c: Perpendicular(g31,g30)
    c: Distance(g30,g32) = 2.2
    c: Distance(g32,g31) = 1.5
    c: PointOnObject(g34,g31)
    c: Distance(g30,g34) = 1.1
    c: Coincident(g34,g2)
    c: Perpendicular(g2,g31)
    c: Coincident(g36,g35)
    c: Coincident(g37,g35)
    c: Coincident(g38,g37)
    c: Coincident(g38,g36)
    c: Parallel(g36,g37)
    c: Parallel(g35,g38)
    c: Perpendicular(g36,g35)
    c: Distance(g35,g37) = 2.2
    c: Distance(g37,g36) = 1.5
    c: PointOnObject(g39,g36)
    c: Distance(g35,g39) = 1.1
    c: Coincident(g39,g4)
    c: Perpendicular(g4,g36)
    c: Coincident(g41,g40)
    c: Coincident(g42,g40)
    c: Coincident(g43,g42)
    c: Coincident(g43,g41)
    c: Parallel(g41,g42)
    c: Parallel(g40,g43)
    c: Perpendicular(g41,g40)
    c: Distance(g40,g42) = 2.2
    c: Distance(g42,g41) = 1.5
    c: PointOnObject(g44,g41)
    c: Distance(g40,g44) = 1.1
    c: Coincident(g5,g44)
    c: Perpendicular(g5,g41)
    c: Coincident(g46,g45)
    c: Coincident(g47,g45)
    c: Coincident(g48,g47)
    c: Coincident(g48,g46)
    c: Parallel(g46,g47)
    c: Parallel(g45,g48)
    c: Perpendicular(g46,g45)
    c: Distance(g45,g47) = 2.2
    c: Distance(g47,g46) = 1.5
    c: PointOnObject(g49,g46)
    c: Distance(g45,g49) = 1.1
    c: Coincident(g49,g6)
    c: Perpendicular(g46,g6)
    c: Coincident(g51,g50)
    c: Coincident(g52,g50)
    c: Coincident(g53,g52)
    c: Coincident(g53,g51)
    c: Parallel(g51,g52)
    c: Parallel(g50,g53)
    c: Perpendicular(g51,g50)
    c: Distance(g50,g52) = 2.2
    c: Distance(g52,g51) = 1.5
    c: PointOnObject(g54,g51)
    c: Distance(g50,g54) = 1.1
    c: Coincident(g54,g7)
    c: Perpendicular(g7,g51)
    c: Coincident(g57,g56)
    c: Coincident(g58,g56)
    c: Coincident(g59,g58)
    c: Coincident(g59,g57)
    c: Parallel(g57,g58)
    c: Parallel(g56,g59)
    c: Perpendicular(g57,g56)
    c: Distance(g56,g58) = 2.2
    c: Distance(g58,g57) = 1.5
    c: PointOnObject(g60,g57)
    c: Distance(g56,g60) = 1.1
    c: Coincident(g60,g55)
    c: Perpendicular(g55,g57)
    c: Equal(g55,g7)
    c: Coincident(g55,g0)
    c: Angle(g55,g7) = 0.261799
    c: Coincident(g62,g61)
    c: Coincident(g63,g61)
    c: Coincident(g64,g63)
    c: Coincident(g64,g62)
    c: Parallel(g62,g63)
    c: Parallel(g61,g64)
    c: Perpendicular(g62,g61)
    c: Distance(g61,g63) = 2.2
    c: Distance(g63,g62) = 1.5
    c: PointOnObject(g65,g62)
    c: Distance(g61,g65) = 1.1
    c: Equal(g7,g66)
    c: Coincident(g66,g65)
    c: Perpendicular(g62,g66)
    c: Coincident(g66,g0)
    c: Angle(g66,g8) = 0.261799
    c: Coincident(g68,g67)
    c: Coincident(g69,g67)
    c: Coincident(g70,g69)
    c: Coincident(g70,g68)
    c: Parallel(g68,g69)
    c: Parallel(g67,g70)
    c: Perpendicular(g68,g67)
    c: Distance(g67,g69) = 2.2
    c: Distance(g69,g68) = 1.5
    c: PointOnObject(g71,g68)
    c: Distance(g67,g71) = 1.1
    c: Perpendicular(g72,g68)
    c: Coincident(g71,g72)
    c: Equal(g72,g66)
    c: Coincident(g72,g0)
    c: Angle(g72,g66) = 0.261799
    c: Coincident(g74,g73)
    c: Coincident(g75,g73)
    c: Coincident(g76,g75)
    c: Coincident(g76,g74)
    c: Parallel(g74,g75)
    c: Parallel(g73,g76)
    c: Perpendicular(g74,g73)
    c: Distance(g73,g75) = 2.2
    c: Distance(g75,g74) = 1.5
    c: PointOnObject(g77,g74)
    c: Distance(g73,g77) = 1.1
    c: Perpendicular(g78,g74)
    c: Coincident(g77,g78)
    c: Equal(g29,g78)
    c: Coincident(g78,g0)
    c: Angle(g29,g78) = 0.261799
    c: Coincident(g79,g73)
    c: Coincident(g79,g73)
    c: Coincident(g80,g79)
    c: Coincident(g80,g75)
    c: Coincident(g81,g80)
    c: Coincident(g81,g74)
    c: Coincident(g82,g24)
    c: Coincident(g82,g81)
    c: Coincident(g83,g82)
    c: Coincident(g83,g24)
    c: Coincident(g84,g83)
    c: Coincident(g84,g26)
    c: Coincident(g85,g84)
    c: Coincident(g85,g25)
    c: Coincident(g86,g85)
    c: Coincident(g86,g18)
    c: Coincident(g87,g86)
    c: Coincident(g87,g18)
    c: Coincident(g88,g87)
    c: Coincident(g88,g20)
    c: Coincident(g89,g88)
    c: Coincident(g89,g19)
    c: Coincident(g90,g89)
    c: Coincident(g90,g30)
    c: Coincident(g91,g90)
    c: Coincident(g91,g30)
    c: Coincident(g92,g91)
    c: Coincident(g92,g32)
    c: Coincident(g93,g92)
    c: Coincident(g93,g31)
    c: Coincident(g94,g93)
    c: Coincident(g94,g9)
    c: Coincident(g95,g94)
    c: PointOnObject(g95,g11)
    c: Vertical(g95)
    c: Coincident(g96,g95)
    c: Coincident(g96,g11)
    c: Coincident(g98,g97)
    c: Coincident(g99,g97)
    c: Coincident(g100,g99)
    c: Coincident(g100,g98)
    c: Parallel(g98,g99)
    c: Parallel(g97,g100)
    c: Perpendicular(g98,g97)
    c: Distance(g97,g99) = 2.2
    c: Distance(g99,g98) = 1.5
    c: PointOnObject(g101,g98)
    c: Distance(g97,g101) = 1.1
    c: Perpendicular(g102,g98)
    c: Coincident(g101,g102)
    c: Coincident(g103,g97)
    c: Coincident(g103,g97)
    c: Coincident(g104,g103)
    c: Coincident(g104,g99)
    c: Coincident(g105,g104)
    c: Coincident(g105,g98)
    c: Equal(g102,g78)
    c: Angle(g78,g102) = 0.261799
    c: Coincident(g107,g106)
    c: Coincident(g108,g106)
    c: Coincident(g109,g108)
    c: Coincident(g109,g107)
    c: Parallel(g107,g108)
    c: Parallel(g106,g109)
    c: Perpendicular(g107,g106)
    c: Distance(g106,g108) = 2.2
    c: Distance(g108,g107) = 1.5
    c: PointOnObject(g110,g107)
    c: Distance(g106,g110) = 1.1
    c: Perpendicular(g111,g107)
    c: Coincident(g110,g111)
    c: Coincident(g112,g108)
    c: Coincident(g113,g112)
    c: Coincident(g113,g107)
    c: Equal(g111,g102)
    c: Angle(g102,g111) = 0.261799
    c: Coincident(g114,g79)
    c: Coincident(g114,g105)
    c: Coincident(g115,g103)
    c: Coincident(g115,g113)
    c: Distance(g117,g118) = 1.1
    c: Coincident(g120,g119)
    c: Coincident(g121,g119)
    c: Coincident(g122,g121)
    c: Coincident(g122,g120)
    c: Parallel(g120,g121)
    c: Parallel(g119,g122)
    c: Perpendicular(g120,g119)
    c: Distance(g119,g121) = 2.2
    c: Distance(g121,g120) = 1.5
    c: PointOnObject(g123,g120)
    c: Distance(g119,g123) = 1.1
    c: Perpendicular(g124,g120)
    c: Angle(g124,g116) = 0.261799
    c: Coincident(g123,g124)
    c: Coincident(g126,g125)
    c: Coincident(g127,g125)
    c: Coincident(g128,g127)
    c: Coincident(g128,g126)
    c: Parallel(g126,g127)
    c: Parallel(g125,g128)
    c: Perpendicular(g126,g125)
    c: Distance(g125,g127) = 2.2
    c: Distance(g127,g126) = 1.5
    c: PointOnObject(g129,g126)
    c: Distance(g125,g129) = 1.1
    c: Perpendicular(g130,g126)
    c: Coincident(g129,g130)
    c: Equal(g130,g124)
    c: Angle(g124,g130) = -0.261799
    c: Coincident(g132,g131)
    c: Coincident(g133,g131)
    c: Coincident(g134,g133)
    c: Coincident(g134,g132)
    c: Parallel(g132,g133)
    c: Parallel(g131,g134)
    c: Perpendicular(g132,g131)
    c: Distance(g131,g133) = 2.2
    c: Distance(g133,g132) = 1.5
    c: PointOnObject(g135,g132)
    c: Distance(g131,g135) = 1.1
    c: Coincident(g135,g116)
    c: Perpendicular(g116,g132)
    c: Coincident(g137,g136)
    c: Coincident(g138,g136)
    c: Coincident(g139,g138)
    c: Coincident(g139,g137)
    c: Parallel(g137,g138)
    c: Parallel(g136,g139)
    c: Perpendicular(g137,g136)
    c: Distance(g136,g138) = 2.2
    c: Distance(g138,g137) = 1.5
    c: PointOnObject(g140,g137)
    c: Distance(g136,g140) = 1.1
    c: Perpendicular(g141,g137)
    c: Coincident(g140,g141)
    c: Equal(g130,g141)
    c: Angle(g130,g141) = -0.261799
    c: Coincident(g142,g136)
    c: Coincident(g142,g136)
    c: Coincident(g143,g142)
    c: Coincident(g143,g138)
    c: Coincident(g144,g143)
    c: Coincident(g144,g137)
    c: Coincident(g145,g125)
    c: Coincident(g145,g144)
    c: Coincident(g146,g145)
    c: Coincident(g146,g125)
    c: Coincident(g147,g146)
    c: Coincident(g147,g127)
    c: Coincident(g148,g147)
    c: Coincident(g148,g126)
    c: Coincident(g149,g148)
    c: Coincident(g149,g119)
    c: Coincident(g150,g149)
    c: Coincident(g150,g119)
    c: Coincident(g151,g150)
    c: Coincident(g151,g121)
    c: Coincident(g152,g151)
    c: Coincident(g152,g120)
    c: Coincident(g153,g152)
    c: Coincident(g153,g131)
    c: Coincident(g154,g153)
    c: Coincident(g154,g131)
    c: Coincident(g155,g154)
    c: Coincident(g155,g133)
    c: Coincident(g156,g155)
    c: Coincident(g156,g132)
    c: Coincident(g157,g156)
    c: Coincident(g157,g117)
    c: Coincident(g159,g158)
    c: Coincident(g160,g158)
    c: Coincident(g161,g160)
    c: Coincident(g161,g159)
    c: Parallel(g159,g160)
    c: Parallel(g158,g161)
    c: Perpendicular(g159,g158)
    c: Distance(g158,g160) = 2.2
    c: Distance(g160,g159) = 1.5
    c: PointOnObject(g162,g159)
    c: Distance(g158,g162) = 1.1
    c: Perpendicular(g163,g159)
    c: Coincident(g162,g163)
    c: Coincident(g164,g159)
    c: Equal(g163,g141)
    c: Angle(g141,g163) = -0.261799
    c: Coincident(g166,g165)
    c: Coincident(g167,g165)
    c: Coincident(g168,g167)
    c: Coincident(g168,g166)
    c: Parallel(g166,g167)
    c: Parallel(g165,g168)
    c: Perpendicular(g166,g165)
    c: Distance(g165,g167) = 2.2
    c: Distance(g167,g166) = 1.5
    c: PointOnObject(g169,g166)
    c: Distance(g165,g169) = 1.1
    c: Perpendicular(g170,g166)
    c: Coincident(g169,g170)
    c: Coincident(g171,g166)
    c: Equal(g170,g163)
    c: Angle(g163,g170) = -0.261799
    c: Coincident(g172,g142)
    c: Coincident(g172,g164)
    c: Coincident(g173,g171)
    c: Coincident(g174,g157)
    c: Coincident(g96,g174)
    c: Coincident(g176,g175)
    c: Coincident(g177,g175)
    c: Parallel(g176,g177)
    c: Perpendicular(g176,g175)
    c: Distance(g175,g177) = 2.2
    c: Distance(g177,g176) = 1.5
    c: PointOnObject(g178,g176)
    c: Distance(g175,g178) = 1.1
    c: Coincident(g180,g179)
    c: Coincident(g181,g179)
    c: Coincident(g182,g181)
    c: Coincident(g182,g180)
    c: Parallel(g180,g181)
    c: Parallel(g179,g182)
    c: Perpendicular(g180,g179)
    c: Distance(g179,g181) = 2.2
    c: Distance(g181,g180) = 1.5
    c: PointOnObject(g183,g180)
    c: Distance(g179,g183) = 1.1
    c: Coincident(g185,g184)
    c: Coincident(g186,g184)
    c: Coincident(g187,g186)
    c: Coincident(g187,g185)
    c: Parallel(g185,g186)
    c: Parallel(g184,g187)
    c: Perpendicular(g185,g184)
    c: Distance(g184,g186) = 2.2
    c: Distance(g186,g185) = 1.5
    c: PointOnObject(g188,g185)
    c: Distance(g184,g188) = 1.1
    c: Coincident(g190,g189)
    c: Coincident(g191,g189)
    c: Coincident(g192,g191)
    c: Coincident(g192,g190)
    c: Parallel(g190,g191)
    c: Parallel(g189,g192)
    c: Perpendicular(g190,g189)
    c: Distance(g189,g191) = 2.2
    c: Distance(g191,g190) = 1.5
    c: PointOnObject(g193,g190)
    c: Distance(g189,g193) = 1.1
    c: Coincident(g195,g194)
    c: Coincident(g196,g194)
    c: Coincident(g197,g196)
    c: Coincident(g197,g195)
    c: Parallel(g195,g196)
    c: Parallel(g194,g197)
    c: Perpendicular(g195,g194)
    c: Distance(g194,g196) = 2.2
    c: Distance(g196,g195) = 1.5
    c: PointOnObject(g198,g195)
    c: Distance(g194,g198) = 1.1
    c: Coincident(g200,g199)
    c: Coincident(g201,g199)
    c: Coincident(g202,g201)
    c: Coincident(g202,g200)
    c: Parallel(g200,g201)
    c: Parallel(g199,g202)
    c: Perpendicular(g200,g199)
    c: Distance(g199,g201) = 2.2
    c: Distance(g201,g200) = 1.5
    c: PointOnObject(g203,g200)
    c: Distance(g199,g203) = 1.1
    c: Coincident(g205,g204)
    c: Coincident(g206,g204)
    c: Coincident(g207,g206)
    c: Coincident(g207,g205)
    c: Parallel(g205,g206)
    c: Parallel(g204,g207)
    c: Perpendicular(g205,g204)
    c: Distance(g204,g206) = 2.2
    c: Distance(g206,g205) = 1.5
    c: PointOnObject(g208,g205)
    c: Distance(g204,g208) = 1.1
    c: Coincident(g210,g209)
    c: Coincident(g211,g209)
    c: Coincident(g212,g211)
    c: Coincident(g212,g210)
    c: Parallel(g210,g211)
    c: Parallel(g209,g212)
    c: Perpendicular(g210,g209)
    c: Distance(g209,g211) = 2.2
    c: Distance(g211,g210) = 1.5
    c: PointOnObject(g213,g210)
    c: Distance(g209,g213) = 1.1
    c: Coincident(g215,g214)
    c: Coincident(g216,g214)
    c: Coincident(g217,g216)
    c: Coincident(g217,g215)
    c: Parallel(g215,g216)
    c: Parallel(g214,g217)
    c: Perpendicular(g215,g214)
    c: Distance(g214,g216) = 2.2
    c: Distance(g216,g215) = 1.5
    c: PointOnObject(g218,g215)
    c: Distance(g214,g218) = 1.1
    c: Coincident(g221,g220)
    c: Coincident(g222,g220)
    c: Coincident(g223,g222)
    c: Coincident(g223,g221)
    c: Parallel(g221,g222)
    c: Parallel(g220,g223)
    c: Perpendicular(g221,g220)
    c: Distance(g220,g222) = 2.2
    c: Distance(g222,g221) = 1.5
    c: PointOnObject(g224,g221)
    c: Distance(g220,g224) = 1.1
    c: Coincident(g225,g220)
    c: Coincident(g225,g220)
    c: Coincident(g226,g225)
    c: Coincident(g226,g222)
    c: Coincident(g227,g226)
    c: Coincident(g227,g221)
    c: Coincident(g228,g189)
    c: Coincident(g228,g227)
    c: Coincident(g229,g228)
    c: Coincident(g229,g189)
    c: Coincident(g230,g229)
    c: Coincident(g230,g191)
    c: Coincident(g231,g230)
    c: Coincident(g231,g190)
    c: Coincident(g232,g231)
    c: Coincident(g232,g184)
    c: Coincident(g233,g232)
    c: Coincident(g233,g184)
    c: Coincident(g234,g233)
    c: Coincident(g234,g186)
    c: Coincident(g235,g234)
    c: Coincident(g235,g185)
    c: Coincident(g236,g235)
    c: Coincident(g236,g194)
    c: Coincident(g237,g236)
    c: Coincident(g237,g194)
    c: Coincident(g238,g237)
    c: Coincident(g238,g196)
    c: Coincident(g239,g238)
    c: Coincident(g239,g195)
    c: Coincident(g240,g239)
    c: Coincident(g240,g175)
    c: Coincident(g241,g240)
    c: PointOnObject(g241,g177)
    c: Coincident(g242,g241)
    c: Coincident(g242,g177)
    c: Coincident(g244,g243)
    c: Coincident(g245,g243)
    c: Coincident(g246,g245)
    c: Coincident(g246,g244)
    c: Parallel(g244,g245)
    c: Parallel(g243,g246)
    c: Perpendicular(g244,g243)
    c: Distance(g243,g245) = 2.2
    c: Distance(g245,g244) = 1.5
    c: PointOnObject(g247,g244)
    c: Distance(g243,g247) = 1.1
    c: Coincident(g248,g243)
    c: Coincident(g248,g243)
    c: Coincident(g249,g248)
    c: Coincident(g249,g245)
    c: Coincident(g250,g249)
    c: Coincident(g250,g244)
    c: Coincident(g253,g225)
    c: Coincident(g253,g250)
    c: Coincident(g254,g248)
    c: Coincident(g254,g252)
    c: Distance(g255,g256) = 1.1
    c: Coincident(g258,g257)
    c: Coincident(g259,g257)
    c: Coincident(g260,g259)
    c: Coincident(g260,g258)
    c: Parallel(g258,g259)
    c: Parallel(g257,g260)
    c: Perpendicular(g258,g257)
    c: Distance(g257,g259) = 2.2
    c: Distance(g259,g258) = 1.5
    c: PointOnObject(g261,g258)
    c: Distance(g257,g261) = 1.1
    c: Coincident(g263,g262)
    c: Coincident(g264,g262)
    c: Coincident(g265,g264)
    c: Coincident(g265,g263)
    c: Parallel(g263,g264)
    c: Parallel(g262,g265)
    c: Perpendicular(g263,g262)
    c: Distance(g262,g264) = 2.2
    c: Distance(g264,g263) = 1.5
    c: PointOnObject(g266,g263)
    c: Distance(g262,g266) = 1.1
    c: Coincident(g268,g267)
    c: Coincident(g269,g267)
    c: Coincident(g270,g269)
    c: Coincident(g270,g268)
    c: Parallel(g268,g269)
    c: Parallel(g267,g270)
    c: Perpendicular(g268,g267)
    c: Distance(g267,g269) = 2.2
    c: Distance(g269,g268) = 1.5
    c: PointOnObject(g271,g268)
    c: Distance(g267,g271) = 1.1
    c: Coincident(g273,g272)
    c: Coincident(g274,g272)
    c: Coincident(g275,g274)
    c: Coincident(g275,g273)
    c: Parallel(g273,g274)
    c: Parallel(g272,g275)
    c: Perpendicular(g273,g272)
    c: Distance(g272,g274) = 2.2
    c: Distance(g274,g273) = 1.5
    c: PointOnObject(g276,g273)
    c: Distance(g272,g276) = 1.1
    c: Coincident(g277,g272)
    c: Coincident(g277,g272)
    c: Coincident(g278,g277)
    c: Coincident(g278,g274)
    c: Coincident(g279,g278)
    c: Coincident(g279,g273)
    c: Coincident(g280,g262)
    c: Coincident(g280,g279)
    c: Coincident(g281,g280)
    c: Coincident(g281,g262)
    c: Coincident(g282,g281)
    c: Coincident(g282,g264)
    c: Coincident(g283,g282)
    c: Coincident(g283,g263)
    c: Coincident(g284,g283)
    c: Coincident(g284,g257)
    c: Coincident(g285,g284)
    c: Coincident(g285,g257)
    c: Coincident(g286,g285)
    c: Coincident(g286,g259)
    c: Coincident(g287,g286)
    c: Coincident(g287,g258)
    c: Coincident(g288,g287)
    c: Coincident(g288,g267)
    c: Coincident(g289,g288)
    c: Coincident(g289,g267)
    c: Coincident(g290,g289)
    c: Coincident(g290,g269)
    c: Coincident(g291,g290)
    c: Coincident(g291,g268)
    c: Coincident(g292,g291)
    c: Coincident(g292,g255)
    c: Coincident(g294,g293)
    c: Coincident(g295,g293)
    c: Coincident(g296,g295)
    c: Coincident(g296,g294)
    c: Parallel(g294,g295)
    c: Parallel(g293,g296)
    c: Perpendicular(g294,g293)
    c: Distance(g293,g295) = 2.2
    c: Distance(g295,g294) = 1.5
    c: PointOnObject(g297,g294)
    c: Distance(g293,g297) = 1.1
    c: Coincident(g298,g293)
    c: Coincident(g298,g293)
    c: Coincident(g299,g298)
    c: Coincident(g299,g295)
    c: Coincident(g300,g299)
    c: Coincident(g300,g294)
    c: Coincident(g302,g277)
    c: Coincident(g302,g300)
    c: Coincident(g303,g298)
    c: Coincident(g304,g292)
    c: Coincident(g242,g304)
    c: Coincident(g305,g-1)
    c: Diameter(g305) = 30
    c: Coincident(g306,g173)
    c: Coincident(g307,g164)
    c: Coincident(g307,g306)
    c: Coincident(g308,g171)
    c: Coincident(g309,g308)
    c: Coincident(g309,g303)
    c: Coincident(g308,g58)
FEATURE [PartDesign::Pad] Pad
  Direction = (1,1,1)
  Length = 3
  Length2 = 100
  Profile = -> Sketch
  Type = 0
FEATURE [PartDesign::Body] Body
  Group = -> [Sketch,Pad]
  Origin = -> Origin
  Tip = -> Pad
